# Revit family: Spec Equip_Soap Dispenser_Argent_Built-in
name_source: partatom
category: Specialty Equipment
revit_build: Autodesk Revit 2016 (Build: 20190508_0715(x64)
units: mm (PartAtom-declared; Revit-internal decimal feet)

## family parameters
Always vertical = Yes
Cut with Voids When Loaded = Yes
OmniClass Number = 23.40.20.21.34
OmniClass Title = Soap Holders, Dispensers
Part Type = Normal
Room Calculation Point = No
Round Connector Dimension = Use Diameter
Shared = No
Work Plane-Based = No

## types (1)
- Chrome (67791)
    Body Material = z_Argent_Chrome
    Bottle Material = z_Argent_Clear Plastic
    Cost = 0 $
    Description = Liquid Soap Dispenser designed for built-in application
    IfcExportAs = IfcSanitaryTerminal
    IfcExportType = NOT DEFINED
    Manufacturer = Argent
    Manufacturer_Overall Depth = 118.12 mm
    Manufacturer_Overall Height = 265 mm
    Manufacturer_Overall Width = 44 mm
    Manufacturer_Spec Code = 67791
    Manufacturer_URL__Product Specific = https://www.argentaust.com.au
    Model = 67791
    ModifiedIssue_ANZRS = 20200402 $
    Type Comments = Chrome Finish
    URL = https://www.argentaust.com.au
    Uniclass2015Code = Pr_40_20_76_82
    Uniclass2015Title = Soap dishes
    Uniclass2015Version = Products v1.17

## geometry (parser evidence)
native form markers: Sweep x1
no freeform markers — native parametric forms only
